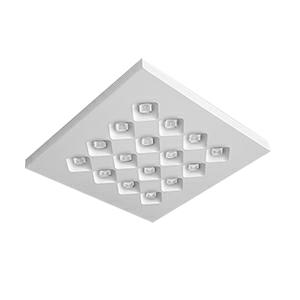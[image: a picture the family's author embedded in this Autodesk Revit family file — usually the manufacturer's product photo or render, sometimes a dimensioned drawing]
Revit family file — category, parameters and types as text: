
# Revit family: 3f_filippi_-_3f_diagon_3f_filippi_-_23098_a0686_-_3f_diagon_25w-930_596x596___corn_plaf__a25b
name_source: partatom
category: Lighting Fixtures
units: mm (PartAtom-declared; Revit-internal decimal feet)

## family parameters
Cut with Voids When Loaded = No
Host = Face
Light Source = No
Part Type = Normal
Room Calculation Point = No
Round Connector Dimension = Use Diameter
Shared = No

## types (1)
- 3F Filippi - 3F Dìagon (1 x LED, 3103 lm, 28 W, 3000 K)
    Apparent Load = 28 VA
    Approval mark = CE
    CIE Flux Codes = 67 96 100 100 100
    Color Rendering = 90
    Color Temperature = 3000 K
    Control Gear = Electronic ballast
    Default Elevation = 1800 mm
    Description = ILLUMINOTECHNICAL
Luminous efficiency 100% (DLOR 100%, ULOR 0%).
Initial luminous flux of the luminaire 3103 lm.
Direct symmetric distribution.
Installation Interdistance Transv.D = 1.39 x hu - Long.D = 1.39 x hu.
Average luminance <1500 cd/m² for radial angles >65°.
Tabular UGR (CIE 117 - 4H-8H; S=0.25H; 70/50/20): RUG 16.3 - 16.2.
Beam angle: 93° - 92°.
Luminous efficacy 111 lm/W.
Lifetime (L95/B10): 30000 h. (tq+25°C)
Lifetime (L90/B10): 50000 h. (tq+25°C)
Lifetime (L80/B10): 80000 h. (tq+25°C)
Lifetime (L75/B10): 100000 h. (tq+25°C)
Sudden decreased luminous flux after 50000 hours: 0% (C0).
Photobiological safety in compliance with IEC/TR 62778: RG0 risk exempt, (IEC 62471).
In compliance with IEC/EN 62722-2-1 - IEC/EN 62717 standards.

SOURCE
Squared LED module 25W/930.
Energy efficiency class (UE 2019/2020 - UE 2019/2015): E.
CIE 13.3 Colour rendering index: CRI >90 (R9 >50%).
IES TM-30 Fidelity Index: Rf = 92 Rg = 101.
CCT nominal colour temperature 3000 K.
Colour initial tolerance (MacAdam): SDCM 3.

MECHANICAL
Housing in hot-galvanised steel, painted in white polyester.
Honeycombed diagonal screen in white anti-glare polycarbonate.
Rhomboidal lenses with differentiated surfaces, etched and prismatic to optimise the orientation of the luminous flux, in transparent methacrylate (PMMA).
Luminaire with limited surface temperature. - D - (EN 60598-2-24)
Dimensions: 600x600 mm, height 40 mm. Weight 6.22 kg.
IP43 protection degree for exposed part, IP20 for recessed part.
Mechanical strength to impacts IK06 (1 joule).
Glow-wire test resistance 650°C.

ELECTRICAL
Halogen Free electronic wiring 230V-50/60Hz, power factor 0.95, THD <25%, constant output current, class I, 1 driver.
Power of the luminaire 28 W.
ENEC - CE.
SAFE FLICKER: PstLM=<1 and SVM=<0.4 (IEC TR 61547-1 and IEC TR 63158), to ensure a more comfortable and safe light.
Luminaire compliant with EN 60598-2-22 for power supply from a centralised emergency system CPSS (Central Power Supply System), not incorporated in the luminaire - high risk areas excluded. The default power and flux are 100% in AC and 100% in DC.
Ambient temperature from 0°C to +25°C.
Temperature class T6 max 85°C.
Quick connection.
Relative humidity UR: <85%.

INSTALLATION
Ceiling.
Height only 40 mm.
All accessories dedicated to this product are available on the Catalog and on our website www.3F-Filippi.com.

ACCESSORIES
A0686 - 596x596 Diagon frame for Ceiling installation.

APPLICATIONS
Environments: staterooms, with VDTs, offices.
Environments with exacting visual tasks, where diffused soft light for optimum visual comfort is required.

WARNING
Luminaire designed for disposal/recycling at end-of-life.
Replaceable (LED only) light source by a professional. Replaceable control gear by a professional.
    Height = 0 mm  [stored 0 ft]
    Lamp = 1 x LED
    Lamp Light Flux = 3103 lm
    Lamp Power = 28 W
    Lamp count = 1
    Length = 600 mm
    Lifetime = 50000 h
    Luminous efficacy = 111 lm/W
    Manufacturer = 3F Filippi
    ModVariant = No
    Model = 3F Filippi - 23098+A0686 - 3F Diagon 25W-930 596x596 + Corn.plaf.
    Mounting Place = Ceiling
    Mounting Type = Recessed
    Number of Poles = 1
    OnlyDefault = Yes
    Power Factor = 1
    Product Name = 3F Filippi - 3F Dìagon
    Product group = recessed luminaire
    ProductGroupID = 4
    Protection Class = Protection class I
    Protection Degree = IP 20
    RLX_Detail_Level = 1
    RLX_Emergency_Light_Flux = 0 lm
    RLX_Emergency_Type = 0
    RLX_Emergency_Type_DB = No
    RlxData = <blob elided: 96161 chars, md5=37fadd3a>
    Socket = socket
    Standby Power = 0 W
    System Light Flux = 3103 lm
    System Power = 28 W
    Type Comments = Product without accessories
    Type Image = 3ffilippi_3f_diagon__a0686.jpg
    URL = http://relux.com
    VarID = ---
    Voltage = 0 V
    Weight = 0.00 kg
    Width = 600 mm

note: [stored X ft] marks values corroborated as IEEE doubles in the binary element streams (Revit-internal decimal feet)

## geometry (parser evidence)
native form markers: Blend x4, Sweep x9
no freeform markers — native parametric forms only
